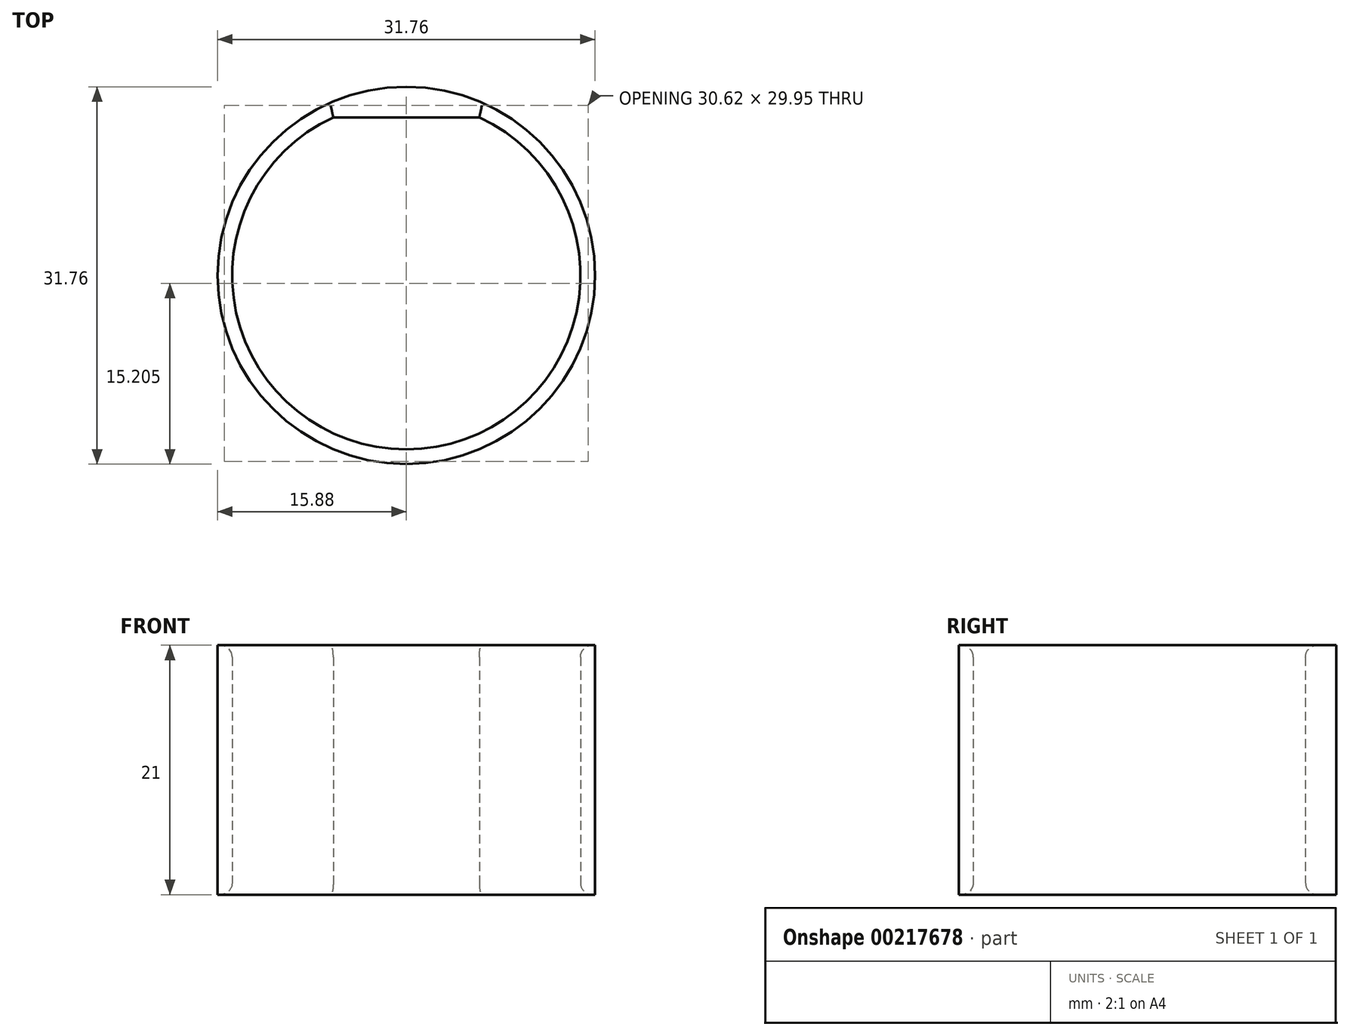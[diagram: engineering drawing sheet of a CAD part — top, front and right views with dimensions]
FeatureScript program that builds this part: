
annotation { "Feature Type Name" : "Feature", "Feature Type Description" : "" }
export const myFeature = defineFeature(function(context is Context, id is Id, definition is map)
    precondition{}
    {
        {
            var Q0;
            Q0=qCreatedBy(makeId("Top.planeOp"),FACE);
            var sketch = newSketch(context, id + "F0", { "sketchPlane" : qUnion([Q0])});
            skCircle(sketch, "E0", {"center": v(0, 0) * mm, "radius": 15.88 * mm});
            skCircle(sketch, "E1", {"center": v(0, 0) * mm, "radius": 14.65 * mm});
            skPoint(sketch, "E2", {"position": v(21.14, 13.3) * mm});
            skLineSegment(sketch, "E3.bottom", {"start": v(-6.14, 13.3) * mm, "end": v(6.14, 13.3) * mm});
            skSolve(sketch);
        }
        {
            var Q0;
            Q0=makeQuery(id+"F0.imprint","IMPRINT",FACE,{"disambiguationData":[TD([[makeQuery(id+"F0.imprint","IMPRINT",EDGE,{"derivedFrom":sQuery(id+"F0.wireOp",EDGE,"E0")}),1.0]])]});
            var Q1;
            {var subQ0=sQuery(id+"F0.wireOp",EDGE,"E3.bottom");var subQ1=sQuery(id+"F0.wireOp",EDGE,"E1");var subQ2=makeQuery(id+"F0.imprint","INTERSECT",VERTEX,{"disambiguationData":[OD(0.0)],"derivedFrom":[subQ1,subQ0]});Q1=makeQuery(id+"F0.imprint","IMPRINT",FACE,{"disambiguationData":[TD([[makeQuery(id+"F0.imprint","IMPRINT",EDGE,{"disambiguationData":[TD([[subQ2,1.0]])],"derivedFrom":subQ1}),1.0]])]});}
            var Q2;
            Q2=makeQuery(id+"F0.imprint","IMPRINT",FACE,{"disambiguationData":[TD([[makeQuery(id+"F0.imprint","IMPRINT",EDGE,{"derivedFrom":sQuery(id+"F0.wireOp",EDGE,"E3.top")}),-1.0]])]});
            extrude(context, id + "F1", {"entities" : qUnion([Q0, Q1, Q2]), "depth" : 21 * mm});
        }
        {
            var Q0;
            Q0=makeQuery(id+"F1.opExtrude","CAP_EDGE",EDGE,{"disambiguationData":[OSD([sQuery(id+"F0.wireOp",EDGE,"E1")])],"isStart":false});
            var Q1;
            Q1=makeQuery(id+"F1.opExtrude","CAP_EDGE",EDGE,{"disambiguationData":[OSD([sQuery(id+"F0.wireOp",EDGE,"E3.bottom")])],"isStart":false});
            var Q2;
            Q2=makeQuery(id+"F1.opExtrude","CAP_EDGE",EDGE,{"disambiguationData":[OSD([sQuery(id+"F0.wireOp",EDGE,"E1")])],"isStart":true});
            var Q3;
            Q3=makeQuery(id+"F1.opExtrude","CAP_EDGE",EDGE,{"disambiguationData":[OSD([sQuery(id+"F0.wireOp",EDGE,"E3.bottom")])],"isStart":true});
            fillet(context, id + "F2", {"entities" : qUnion([Q0, Q1, Q2, Q3]), "radius" : 1 * mm, "tangentPropagation" : true, "allowEdgeOverflow" : false});
        }
    });
